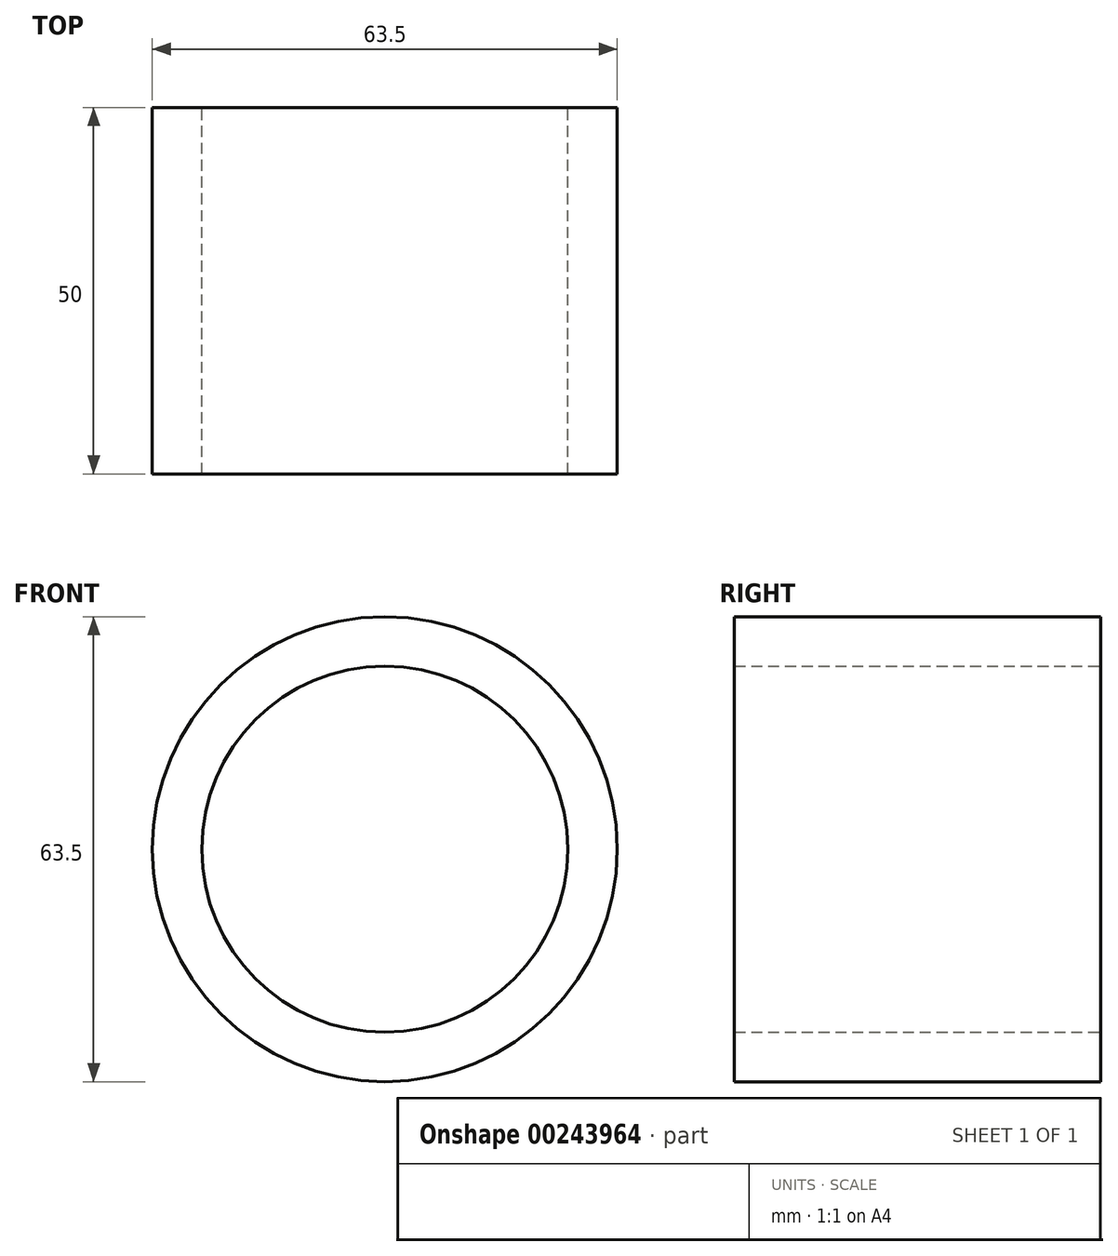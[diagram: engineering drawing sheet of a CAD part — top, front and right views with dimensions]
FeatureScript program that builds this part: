
annotation { "Feature Type Name" : "Feature", "Feature Type Description" : "" }
export const myFeature = defineFeature(function(context is Context, id is Id, definition is map)
    precondition{}
    {
        {
            var Q0;
            Q0=qCreatedBy(makeId("Front.planeOp"),FACE);
            var sketch = newSketch(context, id + "F0", { "sketchPlane" : qUnion([Q0])});
            skCircle(sketch, "E0", {"center": v(0, 0) * mm, "radius": 31.75 * mm});
            skCircle(sketch, "E1", {"center": v(0, 0) * mm, "radius": 25 * mm});
            skSolve(sketch);
        }
        {
            var Q0;
            Q0=makeQuery(id+"F0.imprint","IMPRINT",FACE,{"disambiguationData":[TD([[makeQuery(id+"F0.imprint","IMPRINT",EDGE,{"derivedFrom":sQuery(id+"F0.wireOp",EDGE,"E0")}),1.0]])]});
            extrude(context, id + "F1", {"entities" : qUnion([Q0]), "depth" : 50 * mm});
        }
    });
